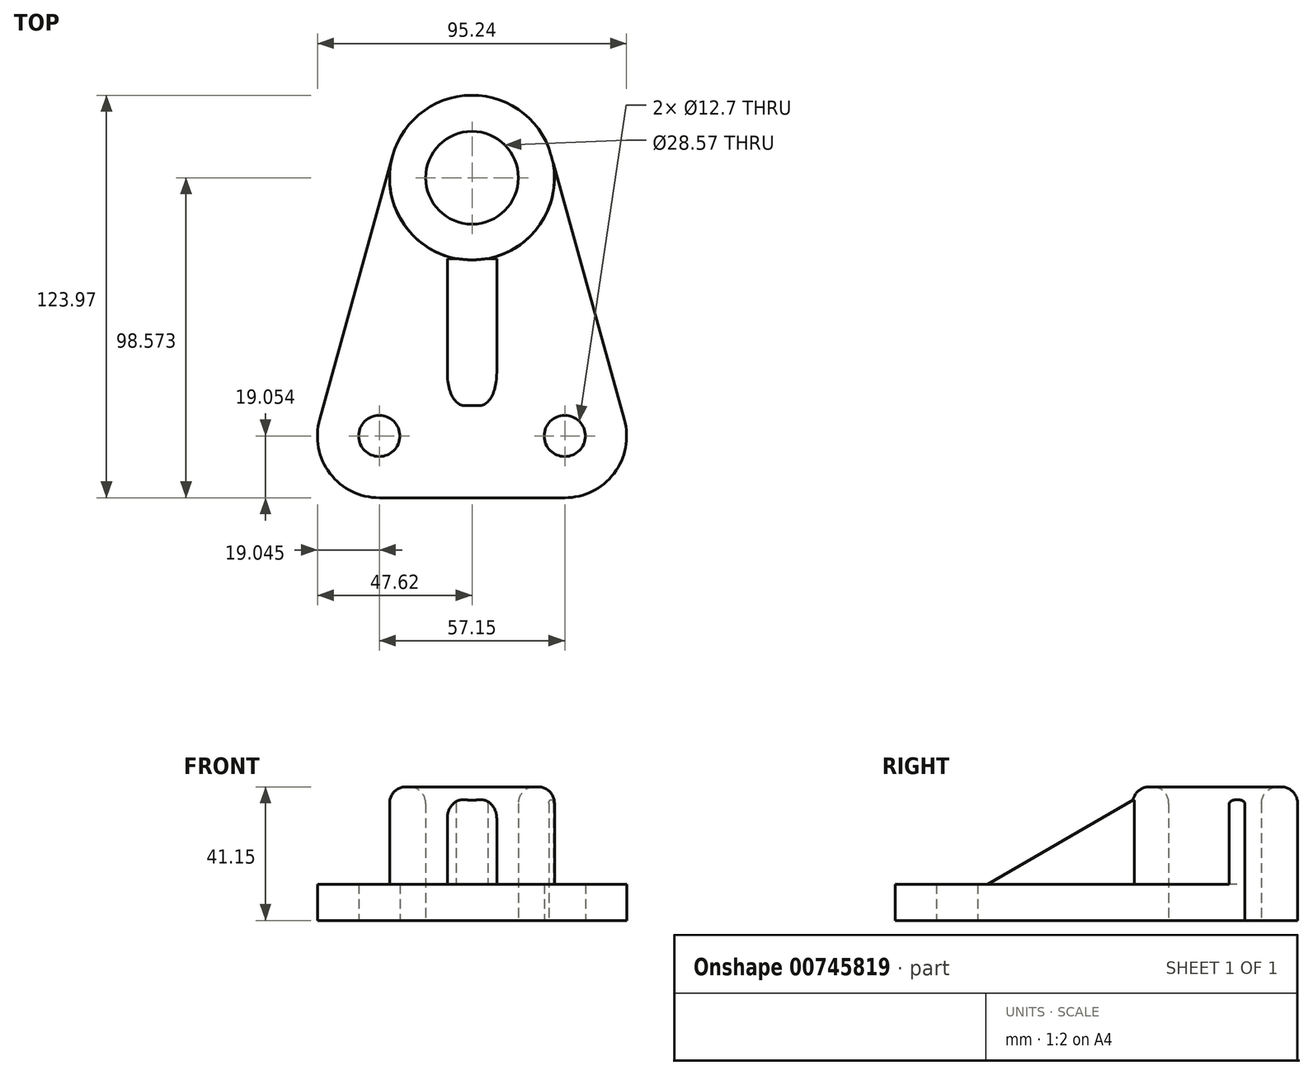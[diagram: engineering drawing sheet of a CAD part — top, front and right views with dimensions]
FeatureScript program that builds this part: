
annotation { "Feature Type Name" : "Feature", "Feature Type Description" : "" }
export const myFeature = defineFeature(function(context is Context, id is Id, definition is map)
    precondition{}
    {
        {
            var Q0;
            Q0=qCreatedBy(makeId("Top.planeOp"),FACE);
            var sketch = newSketch(context, id + "F0", { "sketchPlane" : qUnion([Q0])});
            skCircle(sketch, "E0", {"center": v(0, 38.85) * mm, "radius": 14.29 * mm});
            skCircle(sketch, "E1", {"center": v(0, 38.85) * mm, "radius": 25.4 * mm});
            skCircle(sketch, "E2", {"center": v(-28.57, -40.67) * mm, "radius": 6.35 * mm});
            skCircle(sketch, "E3", {"center": v(28.58, -40.67) * mm, "radius": 6.35 * mm});
            skLineSegment(sketch, "E4", {"start": v(28.58, -40.67) * mm, "end": v(-28.57, -40.67) * mm, "construction": true});
            skLineSegment(sketch, "E5", {"start": v(0, 38.85) * mm, "end": v(0, -40.67) * mm, "construction": true});
            skLineSegment(sketch, "E6", {"start": v(23.7, 48.01) * mm, "end": v(46.93, -35.56) * mm});
            skArc(sketch, "E7", {"start": v(-46.94, -35.59) * mm, "mid": v(-43.73, -52.2) * mm, "end": v(-28.57, -59.72) * mm});
            skArc(sketch, "E8", {"start": v(28.58, -59.72) * mm, "mid": v(43.74, -52.2) * mm, "end": v(46.93, -35.56) * mm});
            skLineSegment(sketch, "E9", {"start": v(-28.57, -59.72) * mm, "end": v(28.58, -59.72) * mm});
            skLineSegment(sketch, "E10", {"start": v(-24.48, 45.62) * mm, "end": v(-46.94, -35.59) * mm});
            skSolve(sketch);
        }
        {
            var Q0;
            Q0=makeQuery(id+"F0.imprint","IMPRINT",FACE,{"disambiguationData":[TD([[makeQuery(id+"F0.imprint","IMPRINT",EDGE,{"derivedFrom":sQuery(id+"F0.wireOp",EDGE,"E0")}),-1.0]])]});
            extrude(context, id + "F1", {"entities" : qUnion([Q0]), "depth" : 41.15 * mm, "offsetDistance" : 25.4 * mm});
        }
        {
            var Q0;
            Q0=makeQuery(id+"F0.imprint","IMPRINT",FACE,{"disambiguationData":[TD([[makeQuery(id+"F0.imprint","IMPRINT",EDGE,{"derivedFrom":sQuery(id+"F0.wireOp",EDGE,"E2")}),-1.0]])]});
            extrude(context, id + "F2", {"entities" : qUnion([Q0]), "operationType" : NewBodyOperationType.ADD, "depth" : 11.18 * mm, "offsetDistance" : 25.4 * mm});
        }
        {
            var Q0;
            Q0=makeQuery(id+"F1.opExtrude","CAP_EDGE",EDGE,{"disambiguationData":[OSD([sQuery(id+"F0.wireOp",EDGE,"E0")])],"isStart":false});
            fillet(context, id + "F3", {"entities" : qUnion([Q0]), "radius" : 5.08 * mm, "tangentPropagation" : true, "allowEdgeOverflow" : false});
        }
        {
            var Q0;
            Q0=qCreatedBy(makeId("Right.planeOp"),FACE);
            var sketch = newSketch(context, id + "F4", { "sketchPlane" : qUnion([Q0])});
            skPoint(sketch, "E11.end.orphan", {"position": v(12.02, 11.38) * mm});
            skLineSegment(sketch, "E12", {"start": v(-30.96, 11.38) * mm, "end": v(-31.3, 11.18) * mm});
            skLineSegment(sketch, "E13", {"start": v(-31.3, 11.18) * mm, "end": v(13.92, 11.18) * mm});
            skLineSegment(sketch, "E14", {"start": v(13.92, 11.18) * mm, "end": v(13.92, 37.29) * mm});
            skPoint(sketch, "E15.start.orphan", {"position": v(12.02, 36.2) * mm});
            skLineSegment(sketch, "E16", {"start": v(13.92, 37.29) * mm, "end": v(-30.96, 11.38) * mm});
            skSolve(sketch);
        }
        {
            var Q0;
            Q0 = qSketchRegion(id + "F4", true);
            extrude(context, id + "F5", {"entities" : qUnion([Q0]), "operationType" : NewBodyOperationType.ADD, "depth" : 15.24 * mm, "offsetDistance" : 25.4 * mm, "symmetric" : true});
        }
        {
            var Q0;
            Q0=makeQuery(id+"F1.opExtrude","CAP_EDGE",EDGE,{"disambiguationData":[OSD([sQuery(id+"F0.wireOp",EDGE,"E1")])],"isStart":false});
            fillet(context, id + "F6", {"entities" : qUnion([Q0]), "radius" : 5.08 * mm, "tangentPropagation" : true, "allowEdgeOverflow" : false});
        }
        {
            var Q0;
            Q0=makeQuery(id+"F5.opExtrude","CAP_EDGE",EDGE,{"disambiguationData":[OSD([sQuery(id+"F4.wireOp",EDGE,"E12"),sQuery(id+"F4.wireOp",EDGE,"E16")])],"isStart":true});
            var Q1;
            Q1=makeQuery(id+"F5.opExtrude","CAP_EDGE",EDGE,{"disambiguationData":[OSD([sQuery(id+"F4.wireOp",EDGE,"E12"),sQuery(id+"F4.wireOp",EDGE,"E16")])],"isStart":false});
            fillet(context, id + "F7", {"entities" : qUnion([Q0, Q1]), "radius" : 5.08 * mm, "tangentPropagation" : true, "allowEdgeOverflow" : false});
        }
    });
